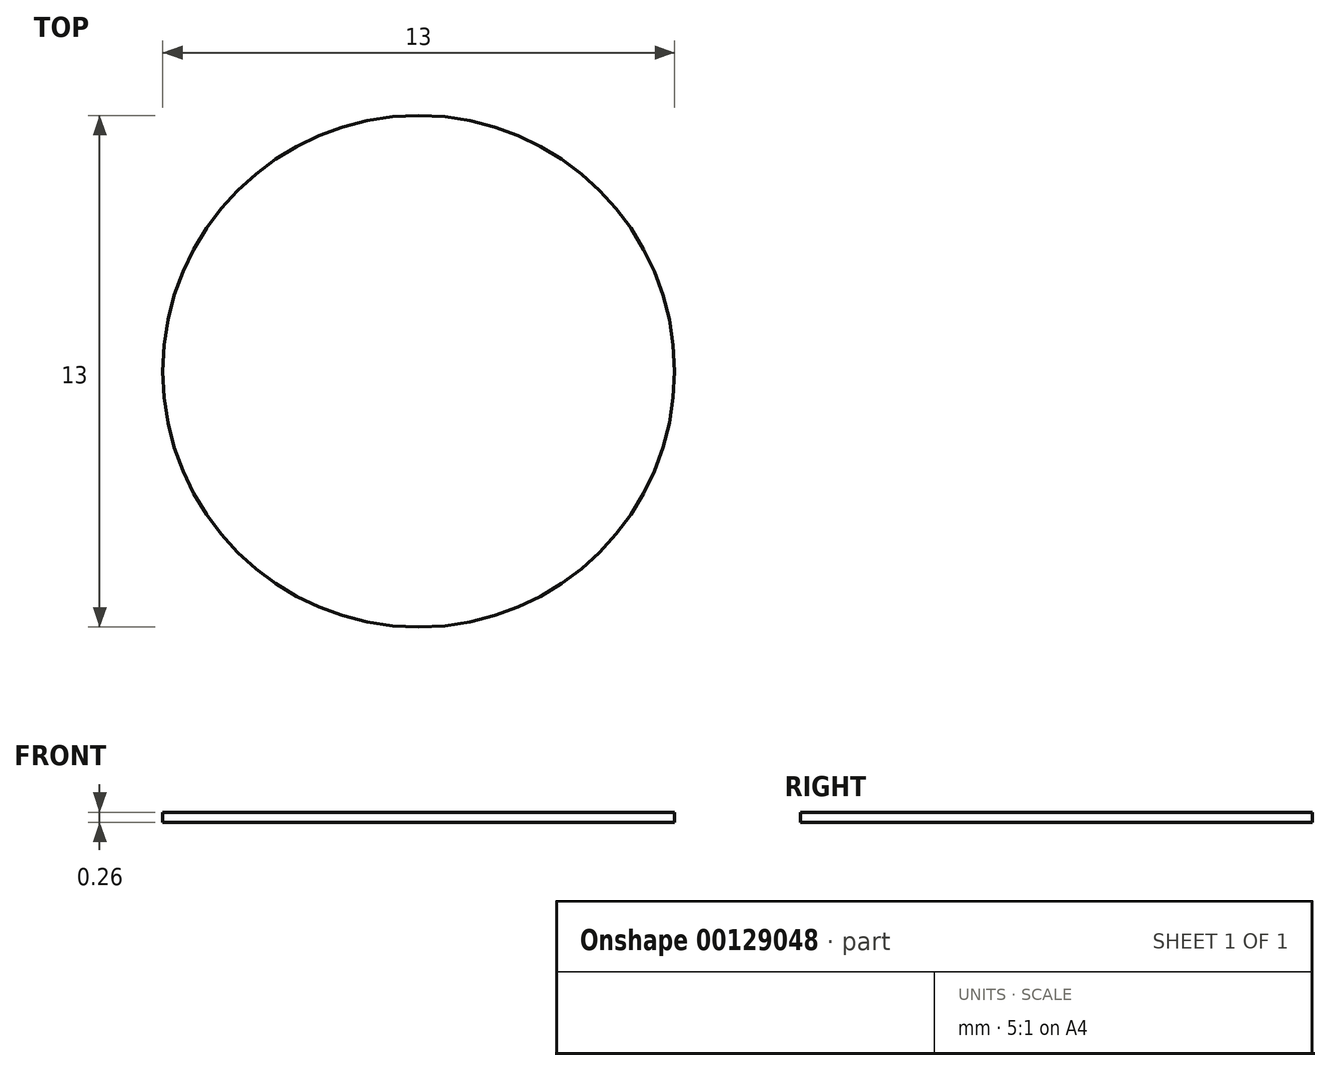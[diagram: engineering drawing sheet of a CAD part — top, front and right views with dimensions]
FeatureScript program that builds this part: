
annotation { "Feature Type Name" : "Feature", "Feature Type Description" : "" }
export const myFeature = defineFeature(function(context is Context, id is Id, definition is map)
    precondition{}
    {
        {
            var Q0;
            Q0=qCreatedBy(makeId("Top.planeOp"),FACE);
            var sketch = newSketch(context, id + "F0", { "sketchPlane" : qUnion([Q0])});
            skCircle(sketch, "E0", {"center": v(0, 0) * mm, "radius": 11.38 * mm});
            skCircle(sketch, "E1", {"center": v(0, 0) * mm, "radius": 6.5 * mm});
            skLineSegment(sketch, "E2", {"start": v(0, 6.5) * mm, "end": v(0, 11.38) * mm});
            skLineSegment(sketch, "E3.1.0", {"start": v(-1.62, 6.3) * mm, "end": v(-2.83, 11.02) * mm});
            skLineSegment(sketch, "E3.2.0", {"start": v(-3.13, 5.7) * mm, "end": v(-5.48, 9.97) * mm});
            skLineSegment(sketch, "E4.1.3.0", {"start": v(-4.45, 4.74) * mm, "end": v(-7.79, 8.3) * mm});
            skLineSegment(sketch, "E4.1.4.0", {"start": v(-5.49, 3.48) * mm, "end": v(-9.6, 6.1) * mm});
            skLineSegment(sketch, "E4.1.5.0", {"start": v(-6.18, 2) * mm, "end": v(-10.82, 3.52) * mm});
            skLineSegment(sketch, "E4.1.6.0", {"start": v(-6.49, 0.4) * mm, "end": v(-11.35, 0.71) * mm});
            skLineSegment(sketch, "E4.1.7.0", {"start": v(-6.38, -1.22) * mm, "end": v(-11.17, -2.13) * mm});
            skLineSegment(sketch, "E4.1.8.0", {"start": v(-5.88, -2.77) * mm, "end": v(-10.3, -4.84) * mm});
            skLineSegment(sketch, "E4.1.9.0", {"start": v(-5, -4.14) * mm, "end": v(-8.76, -7.25) * mm});
            skLineSegment(sketch, "E4.1.10.0", {"start": v(-3.82, -5.26) * mm, "end": v(-6.69, -9.2) * mm});
            skLineSegment(sketch, "E4.1.11.0", {"start": v(-2.4, -6.04) * mm, "end": v(-4.19, -10.58) * mm});
            skLineSegment(sketch, "E4.1.12.0", {"start": v(-0.81, -6.45) * mm, "end": v(-1.43, -11.29) * mm});
            skLineSegment(sketch, "E4.1.13.0", {"start": v(0.81, -6.45) * mm, "end": v(1.43, -11.29) * mm});
            skLineSegment(sketch, "E4.1.14.0", {"start": v(2.4, -6.04) * mm, "end": v(4.19, -10.58) * mm});
            skLineSegment(sketch, "E4.1.15.0", {"start": v(3.82, -5.26) * mm, "end": v(6.69, -9.2) * mm});
            skLineSegment(sketch, "E4.1.16.0", {"start": v(5, -4.14) * mm, "end": v(8.76, -7.25) * mm});
            skLineSegment(sketch, "E4.1.17.0", {"start": v(5.88, -2.77) * mm, "end": v(10.3, -4.84) * mm});
            skLineSegment(sketch, "E4.1.18.0", {"start": v(6.38, -1.22) * mm, "end": v(11.17, -2.13) * mm});
            skLineSegment(sketch, "E4.1.19.0", {"start": v(6.49, 0.4) * mm, "end": v(11.35, 0.71) * mm});
            skLineSegment(sketch, "E4.1.20.0", {"start": v(6.18, 2) * mm, "end": v(10.82, 3.52) * mm});
            skLineSegment(sketch, "E4.1.21.0", {"start": v(5.49, 3.48) * mm, "end": v(9.6, 6.1) * mm});
            skLineSegment(sketch, "E4.1.22.0", {"start": v(4.45, 4.74) * mm, "end": v(7.79, 8.3) * mm});
            skLineSegment(sketch, "E4.1.23.0", {"start": v(3.13, 5.7) * mm, "end": v(5.48, 9.97) * mm});
            skLineSegment(sketch, "E4.1.24.0", {"start": v(1.62, 6.3) * mm, "end": v(2.83, 11.02) * mm});
            skSolve(sketch);
        }
        {
            var Q0;
            {var subQ0=sQuery(id+"F0.wireOp",EDGE,"E1");var subQ19=makeQuery(id+"F0.imprint","INTERSECT",VERTEX,{"derivedFrom":[subQ0,sQuery(id+"F0.wireOp",EDGE,"4c106da2-84de-48f3-a1f3-4199c35ca7dd.1.38.0")]});Q0=makeQuery(id+"F0.imprint","IMPRINT",FACE,{"disambiguationData":[TD([[makeQuery(id+"F0.imprint","IMPRINT",EDGE,{"disambiguationData":[TD([[subQ19,-1.0]])],"derivedFrom":subQ0}),1.0]])]});}
            extrude(context, id + "F1", {"entities" : qUnion([Q0]), "depth" : .26 * mm});
        }
    });
